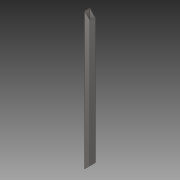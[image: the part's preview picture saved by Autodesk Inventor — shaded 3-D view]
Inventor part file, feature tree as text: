
AUTODESK INVENTOR PART (.ipt)
format: ipt  version: 2019 (Build 230136000, 136)  size: 96,256 bytes
history: native  units: mm
features: extrude x2, sketch x2, projected_geometry x1
ambient origin geometry x8: Origin, YZ Plane, XZ Plane, XY Plane, X Axis, Y Axis, Z Axis, Center Point
bodies: Solid1 (feature_tree)
feature tree (5):
  extrude  "Extrusion1"  Depth=30.0mm
  extrude  "Extrusion2"  Depth=2.5mm
  sketch  "Sketch1"  dims[d0=30.0mm d1=30.0mm]
  sketch  "Sketch2"  dims[d2=2.5mm d3=2.5mm d4=750.0mm d5=0.0mm d6=45.0deg d7=750.0mm d8=0.0mm]
  projected_geometry  "Projected Loop1"
